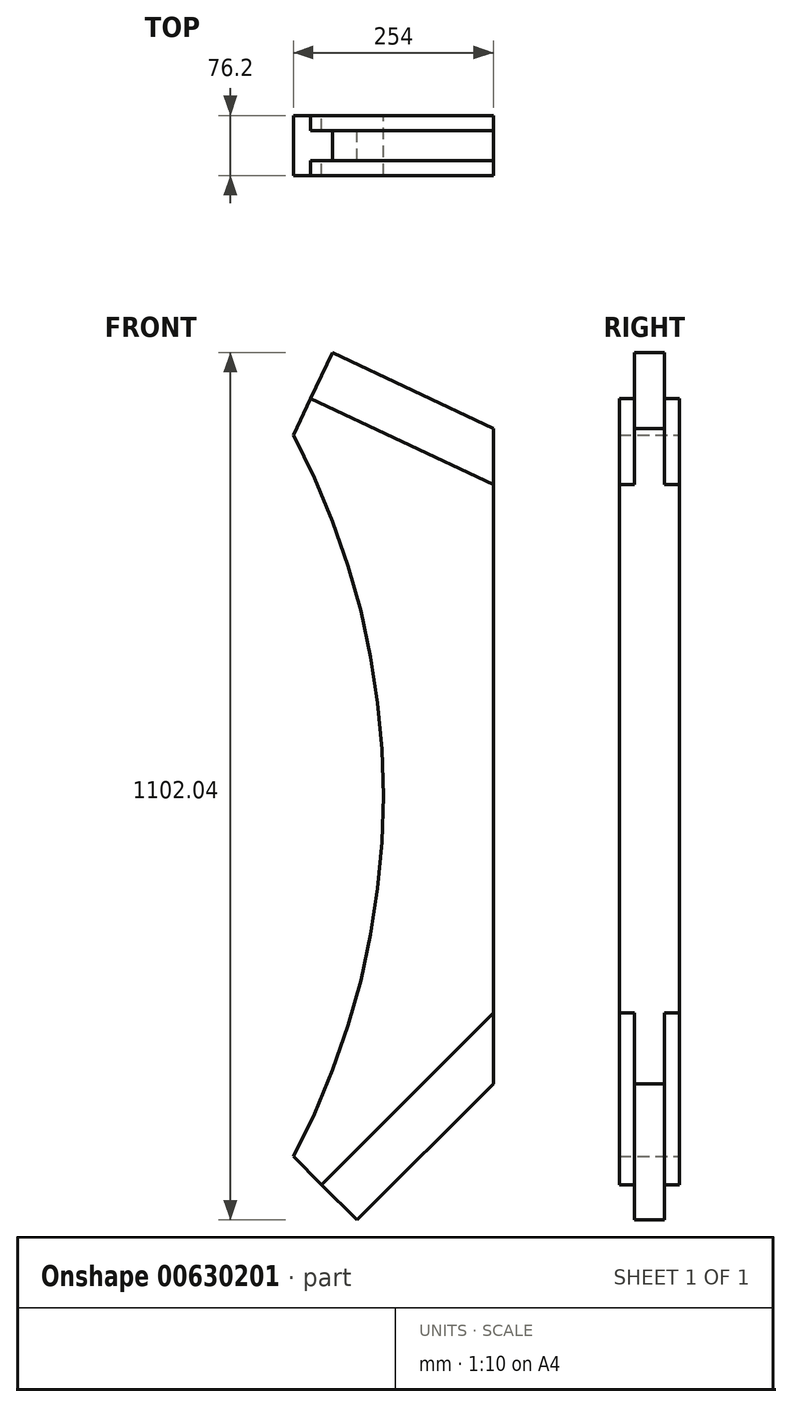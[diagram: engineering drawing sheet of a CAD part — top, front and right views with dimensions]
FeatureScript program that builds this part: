
annotation { "Feature Type Name" : "Feature", "Feature Type Description" : "" }
export const myFeature = defineFeature(function(context is Context, id is Id, definition is map)
    precondition{}
    {
        {
            var Q0;
            Q0=qCreatedBy(makeId("Front.planeOp"),FACE);
            var sketch = newSketch(context, id + "F0", { "sketchPlane" : qUnion([Q0])});
            skLineSegment(sketch, "E0.bottom", {"start": v(-127, 698.5) * mm, "end": v(127, 698.5) * mm});
            skLineSegment(sketch, "E0.top", {"start": v(-127, -698.5) * mm, "end": v(127, -698.5) * mm});
            skLineSegment(sketch, "E0.left", {"start": v(-127, 698.5) * mm, "end": v(-127, -698.5) * mm});
            skLineSegment(sketch, "E0.right", {"start": v(127, 698.5) * mm, "end": v(127, -698.5) * mm});
            skPoint(sketch, "E0.middle", {"position": v(0, 0) * mm});
            skLineSegment(sketch, "E1", {"start": v(127, -283.53) * mm, "end": v(-127, -537.53) * mm});
            skLineSegment(sketch, "E2", {"start": v(-127, -537.53) * mm, "end": v(-46.18, -618.35) * mm});
            skLineSegment(sketch, "E3", {"start": v(-46.18, -618.35) * mm, "end": v(127, -445.17) * mm});
            skLineSegment(sketch, "E4", {"start": v(127, -355.37) * mm, "end": v(-91.08, -573.45) * mm});
            skArc(sketch, "E5", {"start": v(-127, -537.53) * mm, "mid": v(-12.7, -79.3) * mm, "end": v(-127, 378.92) * mm});
            skLineSegment(sketch, "E6", {"start": v(-114.16, 409.57) * mm, "end": v(-109.88, 421.6) * mm});
            skLineSegment(sketch, "E7", {"start": v(-114.16, 409.57) * mm, "end": v(127, 295.3) * mm});
            skLineSegment(sketch, "E8", {"start": v(127, 309.55) * mm, "end": v(-109.88, 421.6) * mm});
            skLineSegment(sketch, "E9", {"start": v(-127, 378.92) * mm, "end": v(-112.79, 408.92) * mm});
            skLineSegment(sketch, "E10", {"start": v(-112.79, 408.92) * mm, "end": v(-80.16, 477.78) * mm});
            skLineSegment(sketch, "E11", {"start": v(-80.16, 477.78) * mm, "end": v(127, 379.63) * mm});
            skLineSegment(sketch, "E12", {"start": v(-110.62, 413.5) * mm, "end": v(127, 302.25) * mm});
            skLineSegment(sketch, "E13", {"start": v(-110.62, 413.5) * mm, "end": v(-126.94, 379.06) * mm});
            skLineSegment(sketch, "E14", {"start": v(-80.16, 477.78) * mm, "end": v(-77.36, 483.7) * mm});
            skLineSegment(sketch, "E15", {"start": v(-77.36, 483.7) * mm, "end": v(127, 386.86) * mm});
            skLineSegment(sketch, "E16", {"start": v(127, 316.27) * mm, "end": v(-105.18, 424.97) * mm});
            skSolve(sketch);
        }
        {
            var Q0;
            {var subQ0=sQuery(id+"F0.wireOp",EDGE,"E7");var subQ1=sQuery(id+"F0.wireOp",EDGE,"E0.right");var subQ2=makeQuery(id+"F0.imprint","INTERSECT",VERTEX,{"derivedFrom":[subQ1,subQ0]});Q0=makeQuery(id+"F0.imprint","IMPRINT",FACE,{"disambiguationData":[TD([[makeQuery(id+"F0.imprint","IMPRINT",EDGE,{"disambiguationData":[TD([[subQ2,1.0]])],"derivedFrom":subQ1}),-1.0]])]});}
            var Q1;
            {var subQ0=sQuery(id+"F0.wireOp",EDGE,"E1");Q1=makeQuery(id+"F0.imprint","IMPRINT",FACE,{"disambiguationData":[TD([[makeQuery(id+"F0.imprint","IMPRINT",EDGE,{"derivedFrom":subQ0}),1.0]])]});}
            var Q2;
            {var subQ4=sQuery(id+"F0.wireOp",EDGE,"E1");Q2=makeQuery(id+"F0.imprint","IMPRINT",FACE,{"disambiguationData":[TD([[makeQuery(id+"F0.imprint","IMPRINT",EDGE,{"derivedFrom":subQ4}),-1.0]])]});}
            var Q3;
            {var subQ3=sQuery(id+"F0.wireOp",EDGE,"E12");Q3=makeQuery(id+"F0.imprint","IMPRINT",FACE,{"disambiguationData":[TD([[makeQuery(id+"F0.imprint","IMPRINT",EDGE,{"derivedFrom":subQ3}),1.0]])]});}
            var Q4;
            {var subQ3=sQuery(id+"F0.wireOp",EDGE,"E16");Q4=makeQuery(id+"F0.imprint","IMPRINT",FACE,{"disambiguationData":[TD([[makeQuery(id+"F0.imprint","IMPRINT",EDGE,{"derivedFrom":subQ3}),1.0]])]});}
            extrude(context, id + "F1", {"entities" : qUnion([Q0, Q1, Q2, Q3, Q4]), "endBound" : BoundingType.SYMMETRIC, "depth" : 76.2 * mm, "offsetDistance" : 25.4 * mm});
        }
        {
            var Q0;
            {var subQ0=sQuery(id+"F0.wireOp",EDGE,"E3");Q0=makeQuery(id+"F0.imprint","IMPRINT",FACE,{"disambiguationData":[TD([[makeQuery(id+"F0.imprint","IMPRINT",EDGE,{"derivedFrom":subQ0}),1.0]])]});}
            var Q1;
            {var subQ3=sQuery(id+"F0.wireOp",EDGE,"E11");Q1=makeQuery(id+"F0.imprint","IMPRINT",FACE,{"disambiguationData":[TD([[makeQuery(id+"F0.imprint","IMPRINT",EDGE,{"derivedFrom":subQ3}),-1.0]])]});}
            var Q2;
            {var subQ3=sQuery(id+"F0.wireOp",EDGE,"E12");Q2=makeQuery(id+"F0.imprint","IMPRINT",FACE,{"disambiguationData":[TD([[makeQuery(id+"F0.imprint","IMPRINT",EDGE,{"derivedFrom":subQ3}),1.0]])]});}
            var Q3;
            {var subQ3=sQuery(id+"F0.wireOp",EDGE,"E16");Q3=makeQuery(id+"F0.imprint","IMPRINT",FACE,{"disambiguationData":[TD([[makeQuery(id+"F0.imprint","IMPRINT",EDGE,{"derivedFrom":subQ3}),1.0]])]});}
            var Q4;
            {var subQ0=sQuery(id+"F0.wireOp",EDGE,"E11");Q4=makeQuery(id+"F0.imprint","IMPRINT",FACE,{"disambiguationData":[TD([[makeQuery(id+"F0.imprint","IMPRINT",EDGE,{"derivedFrom":subQ0}),1.0]])]});}
            extrude(context, id + "F2", {"entities" : qUnion([Q0, Q1, Q2, Q3, Q4]), "operationType" : NewBodyOperationType.ADD, "endBound" : BoundingType.SYMMETRIC, "depth" : 38.1 * mm, "offsetDistance" : 25.4 * mm});
        }
    });
